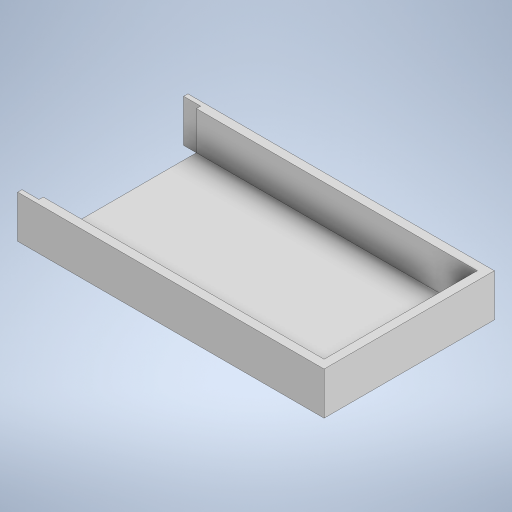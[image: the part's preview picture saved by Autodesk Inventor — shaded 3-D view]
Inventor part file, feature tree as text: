
AUTODESK INVENTOR PART (.ipt)
format: ipt  version: 2023 (Build 270158000, 158)  size: 242,176 bytes
history: native  units: in
note: dims shown in document units (in); Inventor stores cm internally (conversion verified against a paired STEP export)
features: extrude x2, sketch x2, projected_geometry x1
ambient origin geometry x8: Origin, YZ Plane, XZ Plane, XY Plane, X Axis, Y Axis, Z Axis, Center Point
bodies: Volumenkörper1 (feature_tree)
feature tree (5):
  extrude  "Extrusion1"  Depth=0.9843in TaperAngle=0.0deg
  extrude  "Extrusion2"  Depth=0.0984in
  sketch  "Skizze1"  dims[d0=7.0866in d1=3.937in d2=3.5433in d3=6.4961in d4=0.9843in d5=0.0in]
  sketch  "Skizze2"  dims[d6=3.5433in d7=0.0984in d8=6.4961in d9=0.0in d10=0.0197in d11=0.0344in]
  projected_geometry  "Projizierte Kontur1"
